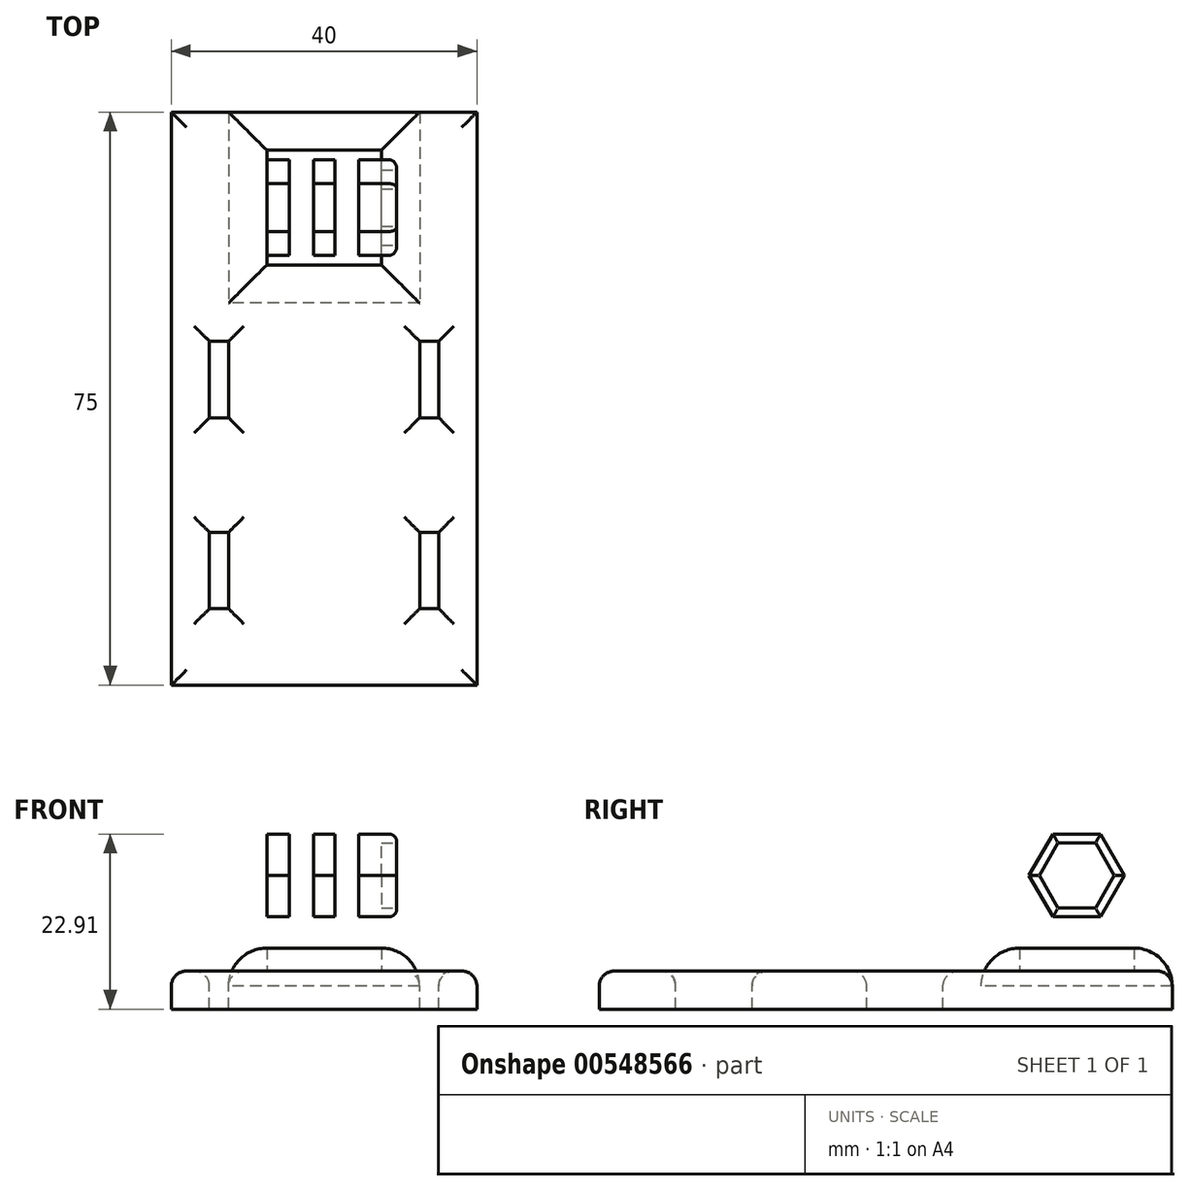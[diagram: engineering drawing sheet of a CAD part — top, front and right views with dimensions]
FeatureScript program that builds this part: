
annotation { "Feature Type Name" : "Feature", "Feature Type Description" : "" }
export const myFeature = defineFeature(function(context is Context, id is Id, definition is map)
    precondition{}
    {
        {
            var Q0;
            Q0=qCreatedBy(makeId("Right.planeOp"),FACE);
            var sketch = newSketch(context, id + "F0", { "sketchPlane" : qUnion([Q0])});
            skPoint(sketch, "E0", {"position": v(0, 12.5) * mm});
            skPoint(sketch, "E1", {"position": v(7.5, 0) * mm});
            skPoint(sketch, "E2.end.orphan", {"position": v(-7.5, 0) * mm});
            skLineSegment(sketch, "E3.top", {"start": v(-7.5, 0) * mm, "end": v(7.5, 0) * mm});
            skLineSegment(sketch, "E3.left", {"start": v(-7.5, 12.5) * mm, "end": v(-7.5, 0) * mm});
            skLineSegment(sketch, "E3.right", {"start": v(7.5, 12.5) * mm, "end": v(7.5, 0) * mm});
            skArc(sketch, "E4", {"start": v(7.5, 12.5) * mm, "mid": v(0, 20) * mm, "end": v(-7.5, 12.5) * mm});
            skCircle(sketch, "E5.cCircle", {"center": v(0, 12.5) * mm, "radius": 4.25 * mm, "construction": true});
            skLineSegment(sketch, "E5.0", {"start": v(-2.45, 16.75) * mm, "end": v(2.45, 16.75) * mm});
            skLineSegment(sketch, "E5.1", {"start": v(2.45, 16.75) * mm, "end": v(4.9, 12.5) * mm});
            skLineSegment(sketch, "E5.2", {"start": v(4.9, 12.5) * mm, "end": v(2.45, 8.25) * mm});
            skLineSegment(sketch, "E5.3", {"start": v(2.45, 8.25) * mm, "end": v(-2.45, 8.25) * mm});
            skLineSegment(sketch, "E5.4", {"start": v(-2.45, 8.25) * mm, "end": v(-4.9, 12.5) * mm});
            skLineSegment(sketch, "E5.5", {"start": v(-4.9, 12.5) * mm, "end": v(-2.45, 16.75) * mm});
            skPoint(sketch, "E5.0.midPoint", {"position": v(0, 16.75) * mm});
            skCircle(sketch, "E6.cCircle", {"center": v(0, 12.5) * mm, "radius": 5.41 * mm, "construction": true});
            skLineSegment(sketch, "E6.0", {"start": v(-3.12, 17.91) * mm, "end": v(3.12, 17.91) * mm});
            skLineSegment(sketch, "E6.1", {"start": v(3.12, 17.91) * mm, "end": v(6.25, 12.5) * mm});
            skLineSegment(sketch, "E6.2", {"start": v(6.25, 12.5) * mm, "end": v(3.12, 7.09) * mm});
            skLineSegment(sketch, "E6.3", {"start": v(3.13, 7.09) * mm, "end": v(-3.12, 7.09) * mm});
            skLineSegment(sketch, "E6.4", {"start": v(-3.12, 7.09) * mm, "end": v(-6.25, 12.5) * mm});
            skLineSegment(sketch, "E6.5", {"start": v(-6.25, 12.5) * mm, "end": v(-3.12, 17.91) * mm});
            skPoint(sketch, "E6.0.midPoint", {"position": v(0, 17.91) * mm});
            skLineSegment(sketch, "E7.top", {"start": v(-7.5, 3) * mm, "end": v(7.5, 3) * mm});
            skLineSegment(sketch, "E7.left", {"start": v(-7.5, 0) * mm, "end": v(-7.5, 3) * mm});
            skLineSegment(sketch, "E7.right", {"start": v(7.5, 0) * mm, "end": v(7.5, 3) * mm});
            skSolve(sketch);
        }
        {
            var Q0;
            Q0=makeQuery(id+"F0.imprint","IMPRINT",FACE,{"disambiguationData":[TD([[makeQuery(id+"F0.imprint","IMPRINT",EDGE,{"derivedFrom":sQuery(id+"F0.wireOp",EDGE,"E3.top")}),1.0]])]});
            extrude(context, id + "F1", {"entities" : qUnion([Q0]), "oppositeDirection" : true, "depth" : 15 * mm});
        }
        {
            var Q0;
            Q0=makeQuery(id+"F0.imprint","IMPRINT",FACE,{"disambiguationData":[TD([[makeQuery(id+"F0.imprint","IMPRINT",EDGE,{"derivedFrom":sQuery(id+"F0.wireOp",EDGE,"E3.left")}),1.0]])]});
            extrude(context, id + "F2", {"entities" : qUnion([Q0]), "operationType" : NewBodyOperationType.ADD, "oppositeDirection" : true, "depth" : 3 * mm});
        }
        {
            var Q0;
            Q0=makeQuery(id+"F0.imprint","IMPRINT",FACE,{"disambiguationData":[TD([[makeQuery(id+"F0.imprint","IMPRINT",EDGE,{"derivedFrom":sQuery(id+"F0.wireOp",EDGE,"E5.0")}),1.0]])]});
            extrude(context, id + "F3", {"entities" : qUnion([Q0]), "operationType" : NewBodyOperationType.ADD, "oppositeDirection" : true, "depth" : 3 * mm});
        }
        {
            var Q0;
            Q0=makeQuery(id+"F0.imprint","IMPRINT",FACE,{"disambiguationData":[TD([[makeQuery(id+"F0.imprint","IMPRINT",EDGE,{"derivedFrom":sQuery(id+"F0.wireOp",EDGE,"E5.0")}),1.0]])]});
            extrude(context, id + "F4", {"entities" : qUnion([Q0]), "operationType" : NewBodyOperationType.ADD, "depth" : 2 * mm});
        }
        {
            var Q0;
            Q0=makeQuery(id+"F0.imprint","IMPRINT",FACE,{"disambiguationData":[TD([[makeQuery(id+"F0.imprint","IMPRINT",EDGE,{"derivedFrom":sQuery(id+"F0.wireOp",EDGE,"E5.0")}),-1.0]])]});
            extrude(context, id + "F5", {"entities" : qUnion([Q0]), "operationType" : NewBodyOperationType.ADD, "oppositeDirection" : true, "depth" : 3 * mm});
        }
        {
            var Q0;
            {var subQ0=sQuery(id+"F0.wireOp",EDGE,"E5.5");var subQ1=sQuery(id+"F0.wireOp",EDGE,"E5.4");var subQ2=sQuery(id+"F0.wireOp",EDGE,"E5.3");var subQ3=sQuery(id+"F0.wireOp",EDGE,"E5.2");var subQ4=sQuery(id+"F0.wireOp",EDGE,"E5.1");var subQ5=sQuery(id+"F0.wireOp",EDGE,"E5.0");var subQ6=sQuery(id+"F0.wireOp",EDGE,"E6.5");var subQ7=sQuery(id+"F0.wireOp",EDGE,"E6.4");var subQ8=sQuery(id+"F0.wireOp",EDGE,"E6.3");var subQ9=sQuery(id+"F0.wireOp",EDGE,"E6.2");var subQ10=sQuery(id+"F0.wireOp",EDGE,"E6.1");var subQ11=sQuery(id+"F0.wireOp",EDGE,"E6.0");Q0=makeQuery(id+"F5.boolean.opBoolean","MERGE",FACE,{"derivedFrom":[makeQuery(id+"F3.boolean.opBoolean","MERGE",FACE,{"derivedFrom":[makeQuery(id+"F2.opExtrude","CAP_FACE",FACE,{"disambiguationData":[OSD([sQuery(id+"F0.wireOp",EDGE,"E3.left"),sQuery(id+"F0.wireOp",EDGE,"E3.right"),sQuery(id+"F0.wireOp",EDGE,"E4"),subQ11,subQ10,subQ9,subQ8,subQ7,subQ6,sQuery(id+"F0.wireOp",EDGE,"E7.top")])],"isStart":false}),makeQuery(id+"F3.opExtrude","CAP_FACE",FACE,{"disambiguationData":[OSD([subQ5,subQ4,subQ3,subQ2,subQ1,subQ0,subQ11,subQ10,subQ9,subQ8,subQ7,subQ6])],"isStart":false})]}),makeQuery(id+"F5.opExtrude","CAP_FACE",FACE,{"disambiguationData":[OSD([subQ5,subQ4,subQ3,subQ2,subQ1,subQ0])],"isStart":false})]});}
            extrude(context, id + "F6", {"entities" : qUnion([Q0]), "operationType" : NewBodyOperationType.ADD, "depth" : 12 * mm});
        }
        {
            var Q0;
            Q0=sQuery(id+"F0.wireOp",VERTEX,"E0");
            var Q1;
            Q1=makeQuery(id+"F1.opExtrude","SWEPT_BODY",BODY,{"disambiguationData":[OSD([sQuery(id+"F0.wireOp",EDGE,"E3.top"),sQuery(id+"F0.wireOp",EDGE,"E7.top"),sQuery(id+"F0.wireOp",EDGE,"E7.left"),sQuery(id+"F0.wireOp",EDGE,"E7.right")])]});
            hole(context, id + "F7", {"style" : HoleStyle.SIMPLE, "endStyle" : HoleEndStyle.BLIND, "holeDiameter" : 5 * mm, "holeDepth" : 15 * mm, "locations" : qUnion([Q0]), "scope" : qUnion([Q1]), "tappedDepth" : 12 * mm, "tapClearance" : 3});
        }
        {
            var Q0;
            Q0=qCreatedBy(makeId("Top.planeOp"),FACE);
            cPlane(context, id + "F8", {"entities" : qUnion([Q0]), "cplaneType" : CPlaneType.OFFSET, "offset" : 20 * mm, "width" : 150 * mm, "height" : 150 * mm});
        }
        {
            var Q0;
            Q0=qCreatedBy(id+"F8.planeOp",FACE);
            var sketch = newSketch(context, id + "F9", { "sketchPlane" : qUnion([Q0])});
            skLineSegment(sketch, "E8.top", {"start": v(0, 7.5) * mm, "end": v(-15, 7.5) * mm});
            skLineSegment(sketch, "E8.left", {"start": v(0, 0) * mm, "end": v(0, 7.5) * mm});
            skLineSegment(sketch, "E8.right", {"start": v(-15, 0) * mm, "end": v(-15, 7.5) * mm});
            skLineSegment(sketch, "E9.top", {"start": v(-15, -7.5) * mm, "end": v(0, -7.5) * mm});
            skLineSegment(sketch, "E9.left", {"start": v(-15, 0) * mm, "end": v(-15, -7.5) * mm});
            skLineSegment(sketch, "E9.right", {"start": v(0, 0) * mm, "end": v(0, -7.5) * mm});
            skLineSegment(sketch, "E10", {"start": v(-7.5, -7.5) * mm, "end": v(-7.5, 7.5) * mm, "construction": true});
            skPoint(sketch, "E11", {"position": v(-6.1, -7.5) * mm});
            skLineSegment(sketch, "E12.bottom", {"start": v(-6.1, -7.5) * mm, "end": v(-8.9, -7.5) * mm});
            skLineSegment(sketch, "E12.top", {"start": v(-6.1, 7.5) * mm, "end": v(-8.9, 7.5) * mm});
            skLineSegment(sketch, "E12.left", {"start": v(-6.1, -7.5) * mm, "end": v(-6.1, 7.5) * mm});
            skLineSegment(sketch, "E12.right", {"start": v(-8.9, -7.5) * mm, "end": v(-8.9, 7.5) * mm});
            skLineSegment(sketch, "E13.bottom", {"start": v(-15, -7.5) * mm, "end": v(-12.05, -7.5) * mm});
            skLineSegment(sketch, "E13.top", {"start": v(-15, 7.5) * mm, "end": v(-12.05, 7.5) * mm});
            skLineSegment(sketch, "E13.left", {"start": v(-15, -7.5) * mm, "end": v(-15, 7.5) * mm});
            skLineSegment(sketch, "E13.right", {"start": v(-12.05, -7.5) * mm, "end": v(-12.05, 7.5) * mm});
            skLineSegment(sketch, "E14.bottom", {"start": v(0, -7.5) * mm, "end": v(-2.95, -7.5) * mm});
            skLineSegment(sketch, "E14.top", {"start": v(0, 7.5) * mm, "end": v(-2.95, 7.5) * mm});
            skLineSegment(sketch, "E14.left", {"start": v(0, -7.5) * mm, "end": v(0, 7.5) * mm});
            skLineSegment(sketch, "E14.right", {"start": v(-2.95, -7.5) * mm, "end": v(-2.95, 7.5) * mm});
            skSolve(sketch);
        }
        {
            var Q0;
            {var subQ2=sQuery(id+"F9.wireOp",EDGE,"E12.right");Q0=makeQuery(id+"F9.imprint","IMPRINT",FACE,{"disambiguationData":[TD([[makeQuery(id+"F9.imprint","IMPRINT",EDGE,{"derivedFrom":subQ2}),1.0]])]});}
            var Q1;
            {var subQ2=sQuery(id+"F9.wireOp",EDGE,"E12.left");Q1=makeQuery(id+"F9.imprint","IMPRINT",FACE,{"disambiguationData":[TD([[makeQuery(id+"F9.imprint","IMPRINT",EDGE,{"derivedFrom":subQ2}),-1.0]])]});}
            extrude(context, id + "F10", {"entities" : qUnion([Q0, Q1]), "operationType" : NewBodyOperationType.REMOVE, "oppositeDirection" : true, "depth" : 17 * mm, "offsetDistance" : 25 * mm});
        }
        {
            var Q0;
            Q0=makeQuery(id+"F4.opExtrude","CAP_EDGE",EDGE,{"disambiguationData":[OSD([sQuery(id+"F0.wireOp",EDGE,"E6.4")])],"isStart":false});
            var Q1;
            Q1=makeQuery(id+"F4.opExtrude","CAP_EDGE",EDGE,{"disambiguationData":[OSD([sQuery(id+"F0.wireOp",EDGE,"E6.3")])],"isStart":false});
            var Q2;
            Q2=makeQuery(id+"F4.opExtrude","CAP_EDGE",EDGE,{"disambiguationData":[OSD([sQuery(id+"F0.wireOp",EDGE,"E6.5")])],"isStart":false});
            var Q3;
            Q3=makeQuery(id+"F4.opExtrude","CAP_EDGE",EDGE,{"disambiguationData":[OSD([sQuery(id+"F0.wireOp",EDGE,"E6.0")])],"isStart":false});
            var Q4;
            Q4=makeQuery(id+"F4.opExtrude","CAP_EDGE",EDGE,{"disambiguationData":[OSD([sQuery(id+"F0.wireOp",EDGE,"E6.1")])],"isStart":false});
            var Q5;
            Q5=makeQuery(id+"F4.opExtrude","CAP_EDGE",EDGE,{"disambiguationData":[OSD([sQuery(id+"F0.wireOp",EDGE,"E6.2")])],"isStart":false});
            fillet(context, id + "F11", {"entities" : qUnion([Q0, Q1, Q2, Q3, Q4, Q5]), "radius" : 1 * mm, "tangentPropagation" : true, "allowEdgeOverflow" : false});
        }
        {
            var Q0;
            Q0=makeQuery(id+"F1.opExtrude","SWEPT_FACE",FACE,{"disambiguationData":[OSD([sQuery(id+"F0.wireOp",EDGE,"E3.top")])]});
            var sketch = newSketch(context, id + "F12", { "sketchPlane" : qUnion([Q0])});
            skLineSegment(sketch, "E15.top", {"start": v(0, -12.5) * mm, "end": v(-27.5, -12.5) * mm});
            skLineSegment(sketch, "E15.left", {"start": v(0, 0) * mm, "end": v(0, -12.5) * mm});
            skLineSegment(sketch, "E15.right", {"start": v(-27.5, 0) * mm, "end": v(-27.5, -12.5) * mm});
            skLineSegment(sketch, "E16.top", {"start": v(0, 62.5) * mm, "end": v(-27.5, 62.5) * mm});
            skLineSegment(sketch, "E16.left", {"start": v(0, 0) * mm, "end": v(0, 62.5) * mm});
            skLineSegment(sketch, "E16.right", {"start": v(-27.5, -20) * mm, "end": v(-27.5, 62.5) * mm});
            skLineSegment(sketch, "E17.bottom", {"start": v(0, 0) * mm, "end": v(12.5, 0) * mm});
            skLineSegment(sketch, "E17.top", {"start": v(0, -12.5) * mm, "end": v(12.5, -12.5) * mm});
            skLineSegment(sketch, "E17.right", {"start": v(12.5, 0) * mm, "end": v(12.5, -12.5) * mm});
            skLineSegment(sketch, "E18.top", {"start": v(0, 62.5) * mm, "end": v(12.5, 62.5) * mm});
            skLineSegment(sketch, "E18.right", {"start": v(12.5, -25) * mm, "end": v(12.5, 62.5) * mm});
            skLineSegment(sketch, "E19.bottom", {"start": v(-20, 27.5) * mm, "end": v(-22.5, 27.5) * mm});
            skLineSegment(sketch, "E19.top", {"start": v(-20, 17.5) * mm, "end": v(-22.5, 17.5) * mm});
            skLineSegment(sketch, "E19.left", {"start": v(-20, 27.5) * mm, "end": v(-20, 17.5) * mm});
            skLineSegment(sketch, "E19.right", {"start": v(-22.5, 27.5) * mm, "end": v(-22.5, 17.5) * mm});
            skPoint(sketch, "E19.middle", {"position": v(-21.25, 22.5) * mm});
            skLineSegment(sketch, "E20.bottom", {"start": v(7.5, 27.5) * mm, "end": v(5, 27.5) * mm});
            skLineSegment(sketch, "E20.top", {"start": v(7.5, 17.5) * mm, "end": v(5, 17.5) * mm});
            skLineSegment(sketch, "E20.left", {"start": v(7.5, 27.5) * mm, "end": v(7.5, 17.5) * mm});
            skLineSegment(sketch, "E20.right", {"start": v(5, 27.5) * mm, "end": v(5, 17.5) * mm});
            skPoint(sketch, "E20.middle", {"position": v(6.25, 22.5) * mm});
            skLineSegment(sketch, "E21.bottom", {"start": v(-20, 52.5) * mm, "end": v(-22.5, 52.5) * mm});
            skLineSegment(sketch, "E21.top", {"start": v(-20, 42.5) * mm, "end": v(-22.5, 42.5) * mm});
            skLineSegment(sketch, "E21.left", {"start": v(-20, 52.5) * mm, "end": v(-20, 42.5) * mm});
            skLineSegment(sketch, "E21.right", {"start": v(-22.5, 52.5) * mm, "end": v(-22.5, 42.5) * mm});
            skPoint(sketch, "E21.middle", {"position": v(-21.25, 47.5) * mm});
            skLineSegment(sketch, "E22.bottom", {"start": v(7.5, 52.5) * mm, "end": v(5, 52.5) * mm});
            skLineSegment(sketch, "E22.top", {"start": v(7.5, 42.5) * mm, "end": v(5, 42.5) * mm});
            skLineSegment(sketch, "E22.left", {"start": v(7.5, 52.5) * mm, "end": v(7.5, 42.5) * mm});
            skLineSegment(sketch, "E22.right", {"start": v(5, 52.5) * mm, "end": v(5, 42.5) * mm});
            skPoint(sketch, "E22.middle", {"position": v(6.25, 47.5) * mm});
            skLineSegment(sketch, "E23", {"start": v(7.5, 52.5) * mm, "end": v(12.5, 52.5) * mm});
            skLineSegment(sketch, "E24", {"start": v(7.5, 17.5) * mm, "end": v(12.5, 17.5) * mm});
            skLineSegment(sketch, "E25", {"start": v(-22.5, 17.5) * mm, "end": v(-27.5, 17.5) * mm});
            skLineSegment(sketch, "E26", {"start": v(-22.5, 42.5) * mm, "end": v(-27.5, 42.5) * mm});
            skLineSegment(sketch, "E27", {"start": v(-20, 27.5) * mm, "end": v(-20, 42.5) * mm});
            skLineSegment(sketch, "E28", {"start": v(-20, 52.5) * mm, "end": v(-20, 62.5) * mm});
            skLineSegment(sketch, "E29", {"start": v(5, 27.5) * mm, "end": v(5, 42.5) * mm});
            skLineSegment(sketch, "E30", {"start": v(5, 52.5) * mm, "end": v(5, 62.5) * mm});
            skSolve(sketch);
        }
        {
            var Q0;
            Q0 = qSketchRegion(id + "F12", true);
            extrude(context, id + "F13", {"entities" : qUnion([Q0]), "depth" : 5 * mm, "offsetDistance" : 25 * mm});
        }
        {
            var Q0;
            Q0=makeQuery(id+"F13.opExtrude","CAP_EDGE",EDGE,{"disambiguationData":[OSD([sQuery(id+"F12.wireOp",EDGE,"E22.bottom")])],"isStart":true});
            var Q1;
            Q1=makeQuery(id+"F13.opExtrude","CAP_EDGE",EDGE,{"disambiguationData":[OSD([sQuery(id+"F12.wireOp",EDGE,"E22.left")])],"isStart":true});
            var Q2;
            Q2=makeQuery(id+"F13.opExtrude","CAP_EDGE",EDGE,{"disambiguationData":[OSD([sQuery(id+"F12.wireOp",EDGE,"E22.top")])],"isStart":true});
            var Q3;
            Q3=makeQuery(id+"F13.opExtrude","CAP_EDGE",EDGE,{"disambiguationData":[OSD([sQuery(id+"F12.wireOp",EDGE,"E22.right")])],"isStart":true});
            fillet(context, id + "F14", {"entities" : qUnion([Q0, Q1, Q2, Q3]), "radius" : 2 * mm, "rho" : 0.5, "crossSection" : FilletCrossSection.CONIC, "allowEdgeOverflow" : false});
        }
        {
            var Q0;
            Q0=makeQuery(id+"F13.opExtrude","CAP_EDGE",EDGE,{"disambiguationData":[OSD([sQuery(id+"F12.wireOp",EDGE,"E21.right")])],"isStart":true});
            var Q1;
            Q1=makeQuery(id+"F13.opExtrude","CAP_EDGE",EDGE,{"disambiguationData":[OSD([sQuery(id+"F12.wireOp",EDGE,"E21.bottom")])],"isStart":true});
            var Q2;
            Q2=makeQuery(id+"F13.opExtrude","CAP_EDGE",EDGE,{"disambiguationData":[OSD([sQuery(id+"F12.wireOp",EDGE,"E21.left")])],"isStart":true});
            var Q3;
            Q3=makeQuery(id+"F13.opExtrude","CAP_EDGE",EDGE,{"disambiguationData":[OSD([sQuery(id+"F12.wireOp",EDGE,"E21.top")])],"isStart":true});
            var Q4;
            Q4=makeQuery(id+"F13.opExtrude","CAP_EDGE",EDGE,{"disambiguationData":[OSD([sQuery(id+"F12.wireOp",EDGE,"E20.right")])],"isStart":true});
            var Q5;
            Q5=makeQuery(id+"F13.opExtrude","CAP_EDGE",EDGE,{"disambiguationData":[OSD([sQuery(id+"F12.wireOp",EDGE,"E20.bottom")])],"isStart":true});
            var Q6;
            Q6=makeQuery(id+"F13.opExtrude","CAP_EDGE",EDGE,{"disambiguationData":[OSD([sQuery(id+"F12.wireOp",EDGE,"E20.left")])],"isStart":true});
            var Q7;
            Q7=makeQuery(id+"F13.opExtrude","CAP_EDGE",EDGE,{"disambiguationData":[OSD([sQuery(id+"F12.wireOp",EDGE,"E20.top")])],"isStart":true});
            var Q8;
            Q8=makeQuery(id+"F13.opExtrude","CAP_EDGE",EDGE,{"disambiguationData":[OSD([sQuery(id+"F12.wireOp",EDGE,"E19.left")])],"isStart":true});
            var Q9;
            Q9=makeQuery(id+"F13.opExtrude","CAP_EDGE",EDGE,{"disambiguationData":[OSD([sQuery(id+"F12.wireOp",EDGE,"E19.bottom")])],"isStart":true});
            var Q10;
            Q10=makeQuery(id+"F13.opExtrude","CAP_EDGE",EDGE,{"disambiguationData":[OSD([sQuery(id+"F12.wireOp",EDGE,"E19.right")])],"isStart":true});
            var Q11;
            Q11=makeQuery(id+"F13.opExtrude","CAP_EDGE",EDGE,{"disambiguationData":[OSD([sQuery(id+"F12.wireOp",EDGE,"E19.top")])],"isStart":true});
            var Q12;
            Q12=makeQuery(id+"F13.opExtrude","CAP_EDGE",EDGE,{"disambiguationData":[OSD([sQuery(id+"F12.wireOp",EDGE,"E17.right"),sQuery(id+"F12.wireOp",EDGE,"E18.right")])],"isStart":true});
            var Q13;
            Q13=makeQuery(id+"F13.opExtrude","CAP_EDGE",EDGE,{"disambiguationData":[OSD([sQuery(id+"F12.wireOp",EDGE,"E15.right"),sQuery(id+"F12.wireOp",EDGE,"E16.right")])],"isStart":true});
            var Q14;
            Q14=makeQuery(id+"F13.opExtrude","CAP_EDGE",EDGE,{"disambiguationData":[OSD([sQuery(id+"F12.wireOp",EDGE,"E15.top"),sQuery(id+"F12.wireOp",EDGE,"E17.top")])],"isStart":true});
            var Q15;
            Q15=makeQuery(id+"F13.opExtrude","CAP_EDGE",EDGE,{"disambiguationData":[OSD([sQuery(id+"F12.wireOp",EDGE,"E16.top"),sQuery(id+"F12.wireOp",EDGE,"E18.top")])],"isStart":true});
            fillet(context, id + "F15", {"entities" : qUnion([Q0, Q1, Q2, Q3, Q4, Q5, Q6, Q7, Q8, Q9, Q10, Q11, Q12, Q13, Q14, Q15]), "radius" : 2 * mm, "tangentPropagation" : true, "allowEdgeOverflow" : false});
        }
        {
            var Q0;
            Q0=makeQuery(id+"F13.opExtrude","CAP_FACE",FACE,{"disambiguationData":[OSD([sQuery(id+"F12.wireOp",EDGE,"E15.top"),sQuery(id+"F12.wireOp",EDGE,"E15.right"),sQuery(id+"F12.wireOp",EDGE,"E16.top"),sQuery(id+"F12.wireOp",EDGE,"E16.right"),sQuery(id+"F12.wireOp",EDGE,"E17.top"),sQuery(id+"F12.wireOp",EDGE,"E17.right"),sQuery(id+"F12.wireOp",EDGE,"E18.top"),sQuery(id+"F12.wireOp",EDGE,"E18.right"),sQuery(id+"F12.wireOp",EDGE,"E19.bottom"),sQuery(id+"F12.wireOp",EDGE,"E19.top"),sQuery(id+"F12.wireOp",EDGE,"E19.left"),sQuery(id+"F12.wireOp",EDGE,"E19.right"),sQuery(id+"F12.wireOp",EDGE,"E20.bottom"),sQuery(id+"F12.wireOp",EDGE,"E20.top"),sQuery(id+"F12.wireOp",EDGE,"E20.left"),sQuery(id+"F12.wireOp",EDGE,"E20.right"),sQuery(id+"F12.wireOp",EDGE,"E21.bottom"),sQuery(id+"F12.wireOp",EDGE,"E21.top"),sQuery(id+"F12.wireOp",EDGE,"E21.left"),sQuery(id+"F12.wireOp",EDGE,"E21.right"),sQuery(id+"F12.wireOp",EDGE,"E22.bottom"),sQuery(id+"F12.wireOp",EDGE,"E22.top"),sQuery(id+"F12.wireOp",EDGE,"E22.left"),sQuery(id+"F12.wireOp",EDGE,"E22.right")])],"isStart":true});
            var sketch = newSketch(context, id + "F16", { "sketchPlane" : qUnion([Q0])});
            skSolve(sketch);
        }
        {
            var Q0;
            {var subQ0=sQuery(id+"F12.wireOp",EDGE,"E22.right");var subQ1=sQuery(id+"F12.wireOp",EDGE,"E22.left");var subQ2=sQuery(id+"F12.wireOp",EDGE,"E22.top");var subQ3=sQuery(id+"F12.wireOp",EDGE,"E22.bottom");var subQ4=sQuery(id+"F12.wireOp",EDGE,"E21.right");var subQ5=sQuery(id+"F12.wireOp",EDGE,"E21.left");var subQ6=sQuery(id+"F12.wireOp",EDGE,"E21.top");var subQ7=sQuery(id+"F12.wireOp",EDGE,"E21.bottom");var subQ8=sQuery(id+"F12.wireOp",EDGE,"E20.right");var subQ9=sQuery(id+"F12.wireOp",EDGE,"E20.left");var subQ10=sQuery(id+"F12.wireOp",EDGE,"E20.top");var subQ11=sQuery(id+"F12.wireOp",EDGE,"E20.bottom");var subQ12=sQuery(id+"F12.wireOp",EDGE,"E19.right");var subQ13=sQuery(id+"F12.wireOp",EDGE,"E19.left");var subQ14=sQuery(id+"F12.wireOp",EDGE,"E19.top");var subQ15=sQuery(id+"F12.wireOp",EDGE,"E19.bottom");var subQ16=sQuery(id+"F12.wireOp",EDGE,"E18.right");var subQ17=sQuery(id+"F12.wireOp",EDGE,"E18.top");var subQ18=sQuery(id+"F12.wireOp",EDGE,"E17.right");var subQ19=sQuery(id+"F12.wireOp",EDGE,"E17.top");var subQ20=sQuery(id+"F12.wireOp",EDGE,"E16.right");var subQ21=sQuery(id+"F12.wireOp",EDGE,"E16.top");var subQ22=sQuery(id+"F12.wireOp",EDGE,"E15.right");var subQ23=sQuery(id+"F12.wireOp",EDGE,"E15.top");var subQ24=makeQuery(id+"F13.opExtrude","CAP_FACE",FACE,{"disambiguationData":[OSD([subQ23,subQ22,subQ21,subQ20,subQ19,subQ18,subQ17,subQ16,subQ15,subQ14,subQ13,subQ12,subQ11,subQ10,subQ9,subQ8,subQ7,subQ6,subQ5,subQ4,subQ3,subQ2,subQ1,subQ0])],"isStart":true});Q0=makeQuery(id+"F16.imprint","IMPRINT",FACE,{"disambiguationData":[TD([[makeQuery(id+"F16.imprint","IMPRINT",EDGE,{"derivedFrom":makeQuery(id+"F14.opFillet","BLEND_EDGE",EDGE,{"blendedFrom":[makeQuery(id+"F13.opExtrude","CAP_EDGE",EDGE,{"disambiguationData":[OSD([subQ3])],"isStart":true}),subQ24],"blendedInto":[subQ24]})}),1.0]])]});}
            var sketch = newSketch(context, id + "F17", { "sketchPlane" : qUnion([Q0])});
            skLineSegment(sketch, "E31.bottom", {"start": v(0, 0) * mm, "end": v(-20, 0) * mm});
            skLineSegment(sketch, "E31.top", {"start": v(0, -12.5) * mm, "end": v(-20, -12.5) * mm});
            skLineSegment(sketch, "E31.left", {"start": v(0, 0) * mm, "end": v(0, -12.5) * mm});
            skLineSegment(sketch, "E31.right", {"start": v(-20, 0) * mm, "end": v(-20, -12.5) * mm});
            skLineSegment(sketch, "E32.top", {"start": v(0, 12.5) * mm, "end": v(-20, 12.5) * mm});
            skLineSegment(sketch, "E32.left", {"start": v(0, 0) * mm, "end": v(0, 12.5) * mm});
            skLineSegment(sketch, "E32.right", {"start": v(-20, 0) * mm, "end": v(-20, 12.5) * mm});
            skLineSegment(sketch, "E33.bottom", {"start": v(0, 0) * mm, "end": v(5, 0) * mm});
            skLineSegment(sketch, "E33.top", {"start": v(0, 12.5) * mm, "end": v(5, 12.5) * mm});
            skLineSegment(sketch, "E33.right", {"start": v(5, 0) * mm, "end": v(5, 12.5) * mm});
            skLineSegment(sketch, "E34.top", {"start": v(0, -12.5) * mm, "end": v(5, -12.5) * mm});
            skLineSegment(sketch, "E34.right", {"start": v(5, 0) * mm, "end": v(5, -12.5) * mm});
            skSolve(sketch);
        }
        {
            var Q0;
            Q0 = qSketchRegion(id + "F17", true);
            extrude(context, id + "F18", {"entities" : qUnion([Q0]), "depth" : 3 * mm, "offsetDistance" : 25 * mm, "hasSecondDirection" : true, "secondDirectionOppositeDirection" : true, "secondDirectionDepth" : 2 * mm});
        }
        {
            var Q0;
            Q0=makeQuery(id+"F18.opExtrude","CAP_EDGE",EDGE,{"disambiguationData":[OSD([sQuery(id+"F17.wireOp",EDGE,"E33.right"),sQuery(id+"F17.wireOp",EDGE,"E34.right")])],"isStart":false});
            var Q1;
            Q1=makeQuery(id+"F18.opExtrude","CAP_EDGE",EDGE,{"disambiguationData":[OSD([sQuery(id+"F17.wireOp",EDGE,"E31.top"),sQuery(id+"F17.wireOp",EDGE,"E34.top")])],"isStart":false});
            var Q2;
            Q2=makeQuery(id+"F18.opExtrude","CAP_EDGE",EDGE,{"disambiguationData":[OSD([sQuery(id+"F17.wireOp",EDGE,"E31.right"),sQuery(id+"F17.wireOp",EDGE,"E32.right")])],"isStart":false});
            var Q3;
            Q3=makeQuery(id+"F18.opExtrude","CAP_EDGE",EDGE,{"disambiguationData":[OSD([sQuery(id+"F17.wireOp",EDGE,"E32.top"),sQuery(id+"F17.wireOp",EDGE,"E33.top")])],"isStart":false});
            fillet(context, id + "F19", {"entities" : qUnion([Q0, Q1, Q2, Q3]), "radius" : 5 * mm, "tangentPropagation" : true, "allowEdgeOverflow" : false});
        }
    });
